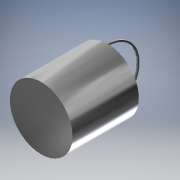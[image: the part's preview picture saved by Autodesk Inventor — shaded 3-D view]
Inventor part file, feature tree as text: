
AUTODESK INVENTOR PART (.ipt)
format: ipt  version: 2017 (Build 210142000, 142)  size: 133,632 bytes
history: native  units: mm
features: extrude x2, sketch x2, shell x1, projected_geometry x1
ambient origin geometry x8: Origin, YZ Plane, XZ Plane, XY Plane, X Axis, Y Axis, Z Axis, Center Point
bodies: Solid1 (feature_tree)
feature tree (6):
  extrude  "Extrusion1"  Depth=180.0mm TaperAngle=0.0deg
  shell  "Shell1"  Thickness=2.0mm
  extrude  "Extrusion2"  Depth=4.0mm TaperAngle=0.0deg
  sketch  "Sketch1"  dims[d0=170.0mm d1=180.0mm d2=0.0mm d3=2.0mm]
  sketch  "Sketch2"  dims[d4=4.0mm d5=4.0mm d6=0.0mm]
  projected_geometry  "Projected Loop1"
